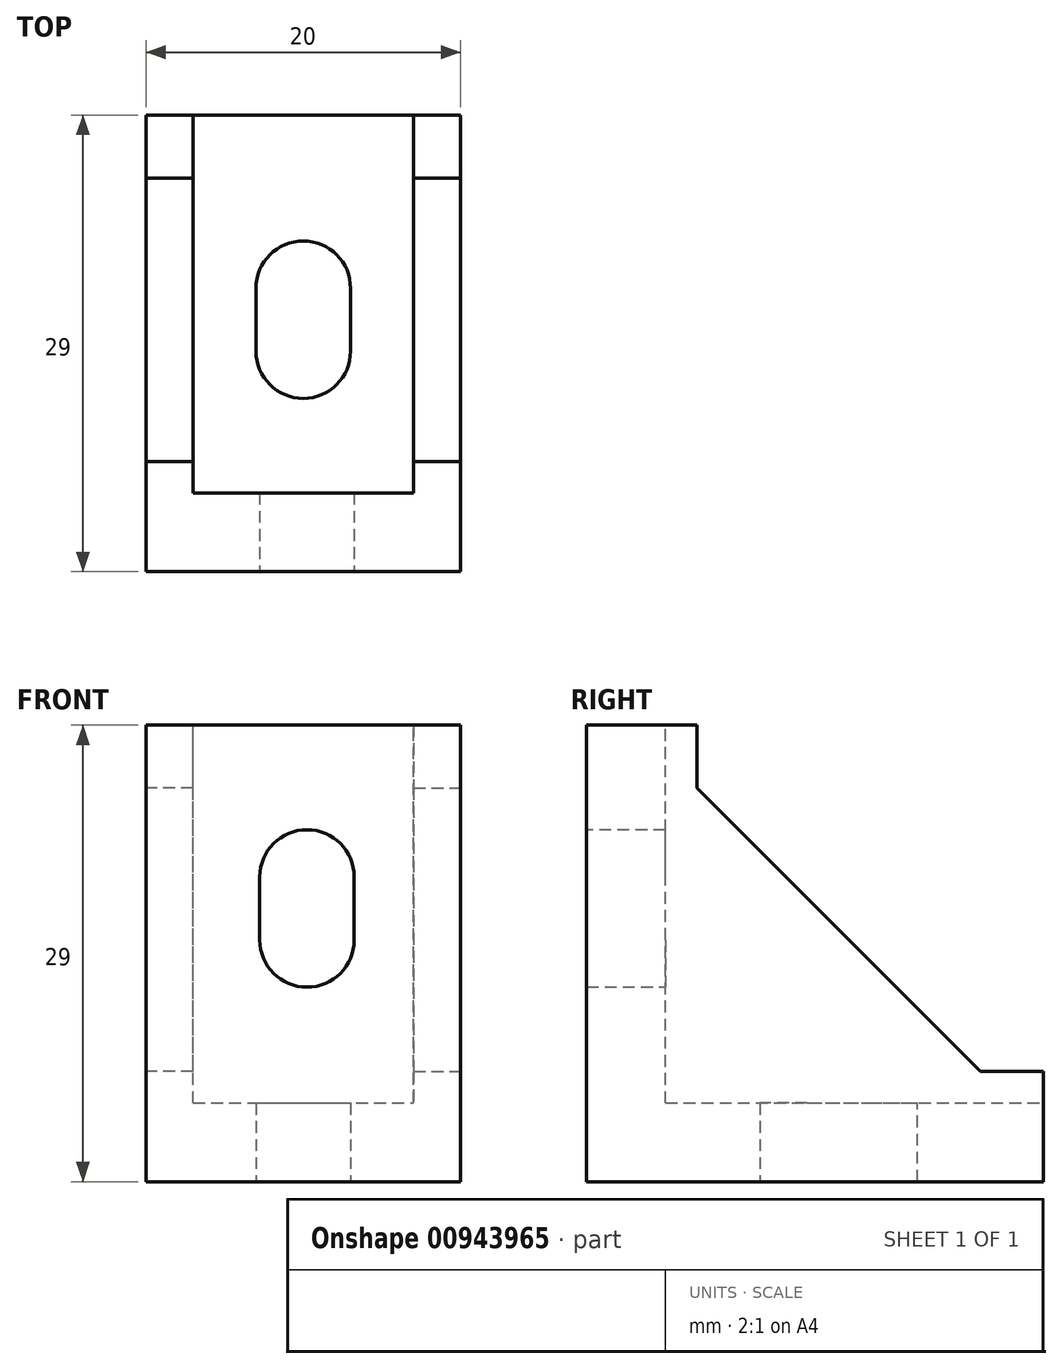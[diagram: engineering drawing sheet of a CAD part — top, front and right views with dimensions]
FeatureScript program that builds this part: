
annotation { "Feature Type Name" : "Feature", "Feature Type Description" : "" }
export const myFeature = defineFeature(function(context is Context, id is Id, definition is map)
    precondition{}
    {
        {
            var Q0;
            Q0=qCreatedBy(makeId("Top.planeOp"),FACE);
            var sketch = newSketch(context, id + "F0", { "sketchPlane" : qUnion([Q0])});
            skLineSegment(sketch, "E0.bottom", {"start": v(0, 0) * mm, "end": v(20, 0) * mm});
            skLineSegment(sketch, "E0.top", {"start": v(0, 29) * mm, "end": v(20, 29) * mm});
            skLineSegment(sketch, "E0.left", {"start": v(0, 0) * mm, "end": v(0, 29) * mm});
            skLineSegment(sketch, "E0.right", {"start": v(20, 0) * mm, "end": v(20, 29) * mm});
            skSolve(sketch);
        }
        {
            var Q0;
            Q0=makeQuery(id+"F0.imprint","IMPRINT",FACE,{"disambiguationData":[TD([[makeQuery(id+"F0.imprint","IMPRINT",EDGE,{"derivedFrom":sQuery(id+"F0.wireOp",EDGE,"E0.bottom")}),1.0]])]});
            extrude(context, id + "F1", {"entities" : qUnion([Q0]), "depth" : 5 * mm, "offsetDistance" : 25 * mm});
        }
        {
            var Q0;
            Q0=makeQuery(id+"F1.opExtrude","SWEPT_FACE",FACE,{"disambiguationData":[OSD([sQuery(id+"F0.wireOp",EDGE,"E0.bottom")])]});
            var sketch = newSketch(context, id + "F2", { "sketchPlane" : qUnion([Q0])});
            skSolve(sketch);
        }
        {
            var Q0;
            {var subQ0=sQuery(id+"F0.wireOp",EDGE,"E0.bottom");Q0=makeQuery(id+"F2.imprint","IMPRINT",FACE,{"disambiguationData":[TD([[makeQuery(id+"F2.imprint","IMPRINT",EDGE,{"derivedFrom":makeQuery(id+"F1.opExtrude","CAP_EDGE",EDGE,{"disambiguationData":[OSD([subQ0])],"isStart":true})}),1.0]])]});}
            var sketch = newSketch(context, id + "F3", { "sketchPlane" : qUnion([Q0])});
            skLineSegment(sketch, "E1.bottom", {"start": v(0, 0) * mm, "end": v(20, 0) * mm});
            skLineSegment(sketch, "E1.top", {"start": v(0, 29) * mm, "end": v(20, 29) * mm});
            skLineSegment(sketch, "E1.left", {"start": v(0, 0) * mm, "end": v(0, 29) * mm});
            skLineSegment(sketch, "E1.right", {"start": v(20, 0) * mm, "end": v(20, 29) * mm});
            skSolve(sketch);
        }
        {
            var Q0;
            {var subQ0=sQuery(id+"F3.wireOp",EDGE,"E1.top");Q0=makeQuery(id+"F3.imprint","IMPRINT",FACE,{"disambiguationData":[TD([[makeQuery(id+"F3.imprint","IMPRINT",EDGE,{"derivedFrom":subQ0}),-1.0]])]});}
            extrude(context, id + "F4", {"entities" : qUnion([Q0]), "operationType" : NewBodyOperationType.ADD, "depth" : -5 * mm, "offsetDistance" : 25 * mm});
        }
        {
            var Q0;
            Q0=makeQuery(id+"F4.boolean.opBoolean","MERGE",FACE,{"derivedFrom":[makeQuery(id+"F1.opExtrude","SWEPT_FACE",FACE,{"disambiguationData":[OSD([sQuery(id+"F0.wireOp",EDGE,"E0.right")])]}),makeQuery(id+"F4.opExtrude","SWEPT_FACE",FACE,{"disambiguationData":[OSD([sQuery(id+"F3.wireOp",EDGE,"E1.right")])]})]});
            var sketch = newSketch(context, id + "F5", { "sketchPlane" : qUnion([Q0])});
            skLineSegment(sketch, "E2", {"start": v(5, 29) * mm, "end": v(7, 29) * mm});
            skLineSegment(sketch, "E3", {"start": v(7, 29) * mm, "end": v(7, 25) * mm});
            skLineSegment(sketch, "E4", {"start": v(7, 25) * mm, "end": v(25, 7) * mm});
            skLineSegment(sketch, "E5", {"start": v(25, 7) * mm, "end": v(29, 7) * mm});
            skLineSegment(sketch, "E6", {"start": v(29, 7) * mm, "end": v(29, 5) * mm});
            skLineSegment(sketch, "E7", {"start": v(29, 5) * mm, "end": v(5, 5) * mm});
            skLineSegment(sketch, "E8", {"start": v(5, 5) * mm, "end": v(5, 29) * mm});
            skSolve(sketch);
        }
        {
            var Q0;
            Q0=makeQuery(id+"F5.imprint","IMPRINT",FACE,{"disambiguationData":[TD([[makeQuery(id+"F5.imprint","IMPRINT",EDGE,{"derivedFrom":sQuery(id+"F5.wireOp",EDGE,"E2")}),-1.0]])]});
            extrude(context, id + "F6", {"entities" : qUnion([Q0]), "operationType" : NewBodyOperationType.ADD, "depth" : -3 * mm, "offsetDistance" : 25 * mm});
        }
        {
            var Q0;
            Q0=makeQuery(id+"F4.boolean.opBoolean","MERGE",FACE,{"derivedFrom":[makeQuery(id+"F1.opExtrude","SWEPT_FACE",FACE,{"disambiguationData":[OSD([sQuery(id+"F0.wireOp",EDGE,"E0.left")])]}),makeQuery(id+"F4.opExtrude","SWEPT_FACE",FACE,{"disambiguationData":[OSD([sQuery(id+"F3.wireOp",EDGE,"E1.left")])]})]});
            var sketch = newSketch(context, id + "F7", { "sketchPlane" : qUnion([Q0])});
            skLineSegment(sketch, "E9.0.0", {"start": v(-29, 0) * mm, "end": v(-29, 7) * mm});
            skLineSegment(sketch, "E9.0.1", {"start": v(-29, 7) * mm, "end": v(-25, 7) * mm});
            skLineSegment(sketch, "E9.0.2", {"start": v(-25, 7) * mm, "end": v(-7, 25) * mm});
            skLineSegment(sketch, "E9.0.3", {"start": v(-7, 25) * mm, "end": v(-7, 29) * mm});
            skLineSegment(sketch, "E9.0.4", {"start": v(-7, 29) * mm, "end": v(0, 29) * mm});
            skLineSegment(sketch, "E9.0.5", {"start": v(0, 29) * mm, "end": v(0, 0) * mm});
            skLineSegment(sketch, "E9.0.6", {"start": v(0, 0) * mm, "end": v(-29, 0) * mm});
            skLineSegment(sketch, "E10", {"start": v(-29, 5) * mm, "end": v(-29, 7) * mm});
            skLineSegment(sketch, "E11", {"start": v(-7, 29) * mm, "end": v(-5, 29) * mm});
            skLineSegment(sketch, "E12", {"start": v(-5, 29) * mm, "end": v(-5, 5) * mm});
            skLineSegment(sketch, "E13", {"start": v(-5, 5) * mm, "end": v(-29, 5) * mm});
            skSolve(sketch);
        }
        {
            var Q0;
            Q0=makeQuery(id+"F7.imprint","IMPRINT",FACE,{"disambiguationData":[TD([[makeQuery(id+"F7.imprint","IMPRINT",EDGE,{"derivedFrom":sQuery(id+"F7.wireOp",EDGE,"E9.0.1")}),-1.0]])]});
            extrude(context, id + "F8", {"entities" : qUnion([Q0]), "operationType" : NewBodyOperationType.ADD, "depth" : -3 * mm, "offsetDistance" : 25 * mm});
        }
        {
            var Q0;
            Q0=makeQuery(id+"F1.opExtrude","CAP_FACE",FACE,{"disambiguationData":[OSD([sQuery(id+"F0.wireOp",EDGE,"E0.bottom"),sQuery(id+"F0.wireOp",EDGE,"E0.top"),sQuery(id+"F0.wireOp",EDGE,"E0.left"),sQuery(id+"F0.wireOp",EDGE,"E0.right")])],"isStart":true});
            var sketch = newSketch(context, id + "F9", { "sketchPlane" : qUnion([Q0])});
            skLineSegment(sketch, "E14.0.0", {"start": v(0, -29) * mm, "end": v(20, -29) * mm});
            skLineSegment(sketch, "E14.0.1", {"start": v(20, -29) * mm, "end": v(20, 0) * mm});
            skLineSegment(sketch, "E14.0.2", {"start": v(20, 0) * mm, "end": v(0, 0) * mm});
            skLineSegment(sketch, "E14.0.3", {"start": v(0, 0) * mm, "end": v(0, -29) * mm});
            skLineSegment(sketch, "E15.bottom", {"start": v(13, -21) * mm, "end": v(7, -21) * mm});
            skLineSegment(sketch, "E15.top", {"start": v(13, -11) * mm, "end": v(7, -11) * mm});
            skLineSegment(sketch, "E15.left", {"start": v(13, -21) * mm, "end": v(13, -11) * mm});
            skLineSegment(sketch, "E15.right", {"start": v(7, -21) * mm, "end": v(7, -11) * mm});
            skPoint(sketch, "E15.middle", {"position": v(10, -16) * mm});
            skPoint(sketch, "E15.middle.positionSnap0", {"position": v(20, -14.5) * mm});
            skPoint(sketch, "E15.middle.positionSnap1", {"position": v(10, -29) * mm});
            skPoint(sketch, "E15.centerSnap0", {"position": v(20, -14.5) * mm});
            skPoint(sketch, "E15.centerSnap1", {"position": v(10, -29) * mm});
            skSolve(sketch);
        }
        {
            var Q0;
            Q0=makeQuery(id+"F9.imprint","IMPRINT",FACE,{"disambiguationData":[TD([[makeQuery(id+"F9.imprint","IMPRINT",EDGE,{"derivedFrom":sQuery(id+"F9.wireOp",EDGE,"E15.bottom")}),-1.0]])]});
            extrude(context, id + "F10", {"entities" : qUnion([Q0]), "operationType" : NewBodyOperationType.REMOVE, "endBound" : BoundingType.THROUGH_ALL, "oppositeDirection" : true, "depth" : 25 * mm, "offsetDistance" : 25 * mm});
        }
        {
            var Q0;
            {var subQ0=sQuery(id+"F0.wireOp",EDGE,"E0.bottom");Q0=makeQuery(id+"F4.boolean.opBoolean","MERGE",FACE,{"derivedFrom":[makeQuery(id+"F1.opExtrude","SWEPT_FACE",FACE,{"disambiguationData":[OSD([subQ0])]}),makeQuery(id+"F4.opExtrude","CAP_FACE",FACE,{"disambiguationData":[OSD([subQ0,sQuery(id+"F3.wireOp",EDGE,"E1.top"),sQuery(id+"F3.wireOp",EDGE,"E1.left"),sQuery(id+"F3.wireOp",EDGE,"E1.right")])],"isStart":true})]});}
            var sketch = newSketch(context, id + "F11", { "sketchPlane" : qUnion([Q0])});
            skLineSegment(sketch, "E16.0.0", {"start": v(0, 0) * mm, "end": v(20, 0) * mm});
            skLineSegment(sketch, "E16.0.1", {"start": v(20, 0) * mm, "end": v(20, 29) * mm});
            skLineSegment(sketch, "E16.0.2", {"start": v(20, 29) * mm, "end": v(0, 29) * mm});
            skLineSegment(sketch, "E16.0.3", {"start": v(0, 29) * mm, "end": v(0, 0) * mm});
            skLineSegment(sketch, "E17.bottom", {"start": v(13.23, 12.35) * mm, "end": v(7.23, 12.35) * mm});
            skLineSegment(sketch, "E17.top", {"start": v(13.23, 22.35) * mm, "end": v(7.23, 22.35) * mm});
            skLineSegment(sketch, "E17.left", {"start": v(13.23, 12.35) * mm, "end": v(13.23, 22.35) * mm});
            skLineSegment(sketch, "E17.right", {"start": v(7.23, 12.35) * mm, "end": v(7.23, 22.35) * mm});
            skPoint(sketch, "E17.middle", {"position": v(10.23, 17.35) * mm});
            skPoint(sketch, "E17.middle.positionSnap0", {"position": v(20, 14.5) * mm});
            skPoint(sketch, "E17.middle.positionSnap1", {"position": v(10.23, 0) * mm});
            skPoint(sketch, "E17.centerSnap0", {"position": v(20, 14.5) * mm});
            skPoint(sketch, "E17.centerSnap1", {"position": v(10.23, 0) * mm});
            skSolve(sketch);
        }
        {
            var Q0;
            Q0=makeQuery(id+"F11.imprint","IMPRINT",FACE,{"disambiguationData":[TD([[makeQuery(id+"F11.imprint","IMPRINT",EDGE,{"derivedFrom":sQuery(id+"F11.wireOp",EDGE,"E17.bottom")}),-1.0]])]});
            extrude(context, id + "F12", {"entities" : qUnion([Q0]), "operationType" : NewBodyOperationType.REMOVE, "endBound" : BoundingType.THROUGH_ALL, "oppositeDirection" : true, "depth" : 25 * mm, "offsetDistance" : 25 * mm});
        }
        {
            var Q0;
            Q0=makeQuery(id+"F10.boolean.opBoolean","COPY",EDGE,{"derivedFrom":makeQuery(id+"F10.opExtrude","SWEPT_EDGE",EDGE,{"disambiguationData":[OSD([sQuery(id+"F9.wireOp",EDGE,"E15.top"),sQuery(id+"F9.wireOp",EDGE,"E15.right")])]})});
            var Q1;
            Q1=makeQuery(id+"F10.boolean.opBoolean","COPY",EDGE,{"derivedFrom":makeQuery(id+"F10.opExtrude","SWEPT_EDGE",EDGE,{"disambiguationData":[OSD([sQuery(id+"F9.wireOp",EDGE,"E15.top"),sQuery(id+"F9.wireOp",EDGE,"E15.left")])]})});
            var Q2;
            Q2=makeQuery(id+"F10.boolean.opBoolean","COPY",EDGE,{"derivedFrom":makeQuery(id+"F10.opExtrude","SWEPT_EDGE",EDGE,{"disambiguationData":[OSD([sQuery(id+"F9.wireOp",EDGE,"E15.bottom"),sQuery(id+"F9.wireOp",EDGE,"E15.right")])]})});
            var Q3;
            Q3=makeQuery(id+"F10.boolean.opBoolean","COPY",EDGE,{"derivedFrom":makeQuery(id+"F10.opExtrude","SWEPT_EDGE",EDGE,{"disambiguationData":[OSD([sQuery(id+"F9.wireOp",EDGE,"E15.bottom"),sQuery(id+"F9.wireOp",EDGE,"E15.left")])]})});
            var Q4;
            Q4=makeQuery(id+"F12.boolean.opBoolean","COPY",EDGE,{"derivedFrom":makeQuery(id+"F12.opExtrude","SWEPT_EDGE",EDGE,{"disambiguationData":[OSD([sQuery(id+"F11.wireOp",EDGE,"E17.bottom"),sQuery(id+"F11.wireOp",EDGE,"E17.right")])]})});
            var Q5;
            Q5=makeQuery(id+"F12.boolean.opBoolean","COPY",EDGE,{"derivedFrom":makeQuery(id+"F12.opExtrude","SWEPT_EDGE",EDGE,{"disambiguationData":[OSD([sQuery(id+"F11.wireOp",EDGE,"E17.bottom"),sQuery(id+"F11.wireOp",EDGE,"E17.left")])]})});
            var Q6;
            Q6=makeQuery(id+"F12.boolean.opBoolean","COPY",EDGE,{"derivedFrom":makeQuery(id+"F12.opExtrude","SWEPT_EDGE",EDGE,{"disambiguationData":[OSD([sQuery(id+"F11.wireOp",EDGE,"E17.top"),sQuery(id+"F11.wireOp",EDGE,"E17.right")])]})});
            var Q7;
            Q7=makeQuery(id+"F12.boolean.opBoolean","COPY",EDGE,{"derivedFrom":makeQuery(id+"F12.opExtrude","SWEPT_EDGE",EDGE,{"disambiguationData":[OSD([sQuery(id+"F11.wireOp",EDGE,"E17.top"),sQuery(id+"F11.wireOp",EDGE,"E17.left")])]})});
            fillet(context, id + "F13", {"entities" : qUnion([Q0, Q1, Q2, Q3, Q4, Q5, Q6, Q7]), "radius" : 3 * mm, "tangentPropagation" : true, "allowEdgeOverflow" : false});
        }
    });
